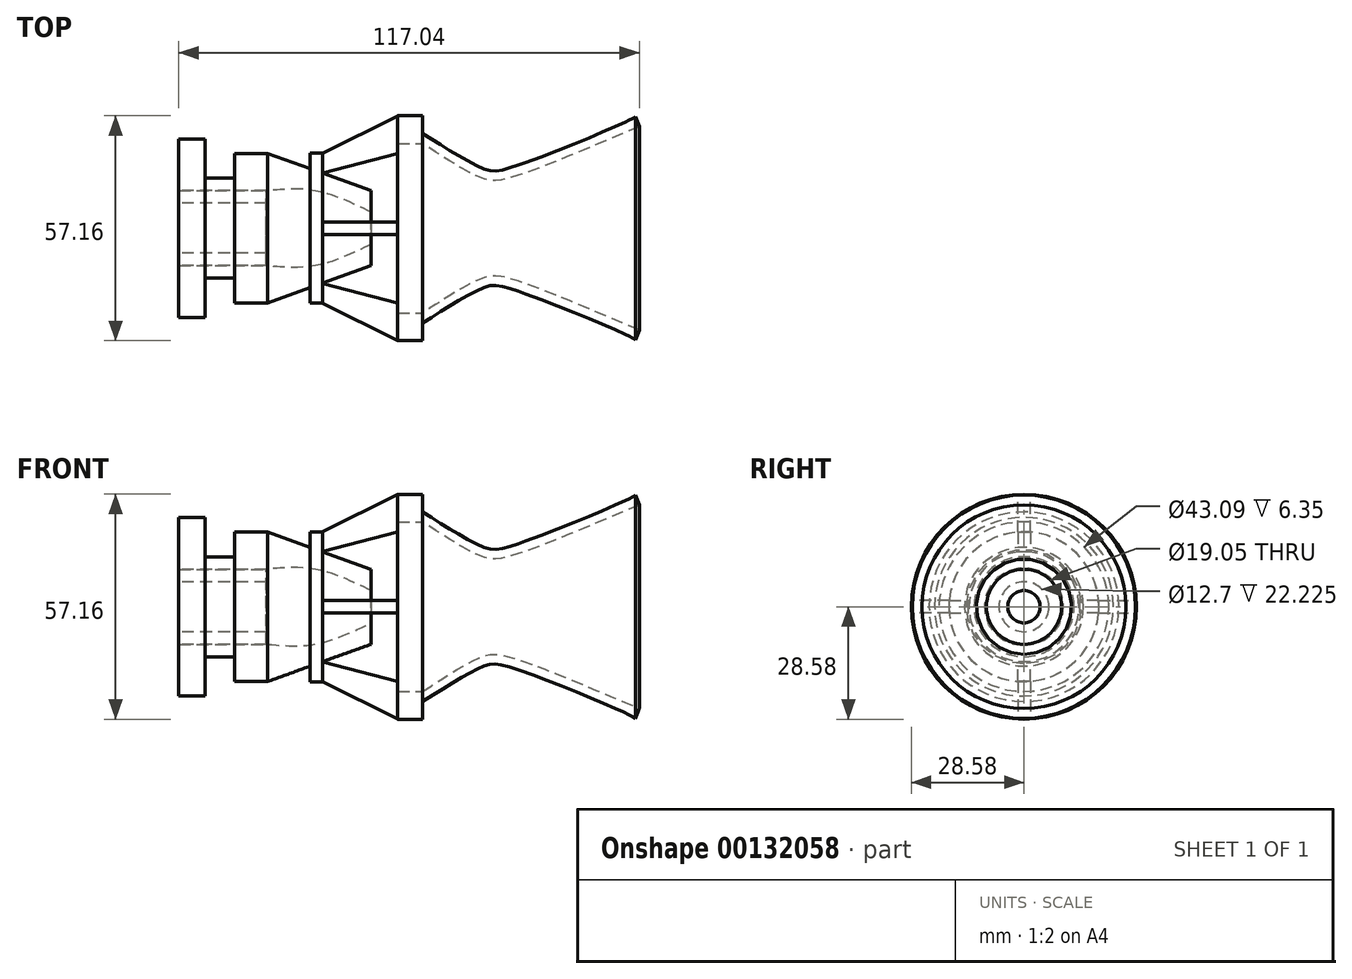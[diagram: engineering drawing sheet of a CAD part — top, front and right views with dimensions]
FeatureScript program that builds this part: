
annotation { "Feature Type Name" : "Feature", "Feature Type Description" : "" }
export const myFeature = defineFeature(function(context is Context, id is Id, definition is map)
    precondition{}
    {
        {
            var Q0;
            Q0=qCreatedBy(makeId("Front.planeOp"),FACE);
            var sketch = newSketch(context, id + "F0", { "sketchPlane" : qUnion([Q0])});
            skPoint(sketch, "E0.middle", {"position": v(0, 0) * mm});
            skLineSegment(sketch, "E1", {"start": v(0, 0) * mm, "end": v(0, 21.54) * mm, "construction": true});
            skPoint(sketch, "E2", {"position": v(0, 21.54) * mm});
            skPoint(sketch, "E3", {"position": v(15.15, 12.7) * mm});
            skPoint(sketch, "E4", {"position": v(21.84, 12.7) * mm});
            skPoint(sketch, "E5", {"position": v(40.5, 25.89) * mm});
            skFitSpline(sketch, "E6", {"points": [v(0, 21.54) * mm, v(15.15, 12.7) * mm, v(21.84, 12.7) * mm, v(55.06, 25.89) * mm], "startDerivative": vector(52.15, -34.15) * mm, "endDerivative": vector(85.37, 36.4) * mm});
            skPoint(sketch, "E7.0.1.0", {"position": v(0, 24.13) * mm});
            skPoint(sketch, "E7.1.1.0", {"position": v(25.4, 24.13) * mm});
            skPoint(sketch, "E7.2.1.0", {"position": v(50.8, 24.13) * mm});
            skLineSegment(sketch, "E7.direction2", {"start": v(0, 24.08) * mm, "end": v(0, 24.13) * mm, "construction": true});
            skPoint(sketch, "E8.1.0.0", {"position": v(21.84, 15.24) * mm});
            skPoint(sketch, "E8.1.0.1", {"position": v(50.8, 26.67) * mm});
            skPoint(sketch, "E8.1.0.2", {"position": v(15.15, 15.24) * mm});
            skPoint(sketch, "E8.1.0.3", {"position": v(25.4, 26.67) * mm});
            skPoint(sketch, "E8.1.0.4", {"position": v(40.5, 28.43) * mm});
            skPoint(sketch, "E8.1.0.5", {"position": v(0, 26.67) * mm});
            skPoint(sketch, "E8.1.0.6", {"position": v(0, 24.08) * mm});
            skLineSegment(sketch, "E8.1.0.7", {"start": v(0, 24.08) * mm, "end": v(0, 26.67) * mm, "construction": true});
            skFitSpline(sketch, "E9", {"points": [v(0, 24.08) * mm, v(15.15, 15.24) * mm, v(21.84, 15.24) * mm, v(50.8, 26.67) * mm, v(54.12, 28.35) * mm], "startDerivative": vector(59.62, -37.76) * mm, "endDerivative": vector(15.17, 8.75) * mm});
            skLineSegment(sketch, "E10", {"start": v(54.12, 28.35) * mm, "end": v(55.06, 25.89) * mm});
            skLineSegment(sketch, "E11", {"start": v(0, 0) * mm, "end": v(0, 21.54) * mm});
            skLineSegment(sketch, "E12", {"start": v(0, 28.58) * mm, "end": v(-6.35, 28.58) * mm});
            skLineSegment(sketch, "E13", {"start": v(-6.35, 28.58) * mm, "end": v(-6.35, 21.54) * mm});
            skLineSegment(sketch, "E14", {"start": v(-6.35, 21.54) * mm, "end": v(0, 21.54) * mm});
            skLineSegment(sketch, "E15", {"start": v(-25.4, 19.05) * mm, "end": v(-28.58, 19.05) * mm});
            skLineSegment(sketch, "E16", {"start": v(-28.58, 19.05) * mm, "end": v(-28.58, 15.1) * mm});
            skPoint(sketch, "E17.startSnap0", {"position": v(-28.58, 9.53) * mm});
            skLineSegment(sketch, "E18", {"start": v(-39.44, 19.02) * mm, "end": v(-47.76, 19.02) * mm});
            skLineSegment(sketch, "E19", {"start": v(-47.76, 19.02) * mm, "end": v(-47.76, 12.7) * mm});
            skLineSegment(sketch, "E20", {"start": v(-47.76, 12.7) * mm, "end": v(-55.22, 12.7) * mm});
            skLineSegment(sketch, "E21", {"start": v(-55.22, 12.7) * mm, "end": v(-55.22, 22.7) * mm});
            skLineSegment(sketch, "E22", {"start": v(-55.22, 22.7) * mm, "end": v(-61.98, 22.7) * mm});
            skLineSegment(sketch, "E23", {"start": v(-61.98, 22.7) * mm, "end": v(-61.98, 12.7) * mm});
            skLineSegment(sketch, "E24", {"start": v(-61.98, 12.7) * mm, "end": v(-61.98, 9.53) * mm});
            skLineSegment(sketch, "E25", {"start": v(-61.98, 9.53) * mm, "end": v(-39.44, 9.53) * mm});
            skPoint(sketch, "E26.1.internal.snap0", {"position": v(-25.4, 9.53) * mm});
            skFitSpline(sketch, "E26", {"points": [v(-39.44, 9.53) * mm, v(-27.3, 9.53) * mm, v(-13.09, 4.11) * mm], "startDerivative": vector(25.44, 2.42) * mm, "endDerivative": vector(27.23, -12.96) * mm});
            skLineSegment(sketch, "E27", {"start": v(-13.09, 4.11) * mm, "end": v(-13.09, 9.53) * mm});
            skLineSegment(sketch, "E28", {"start": v(-13.09, 9.53) * mm, "end": v(-25.4, 13.96) * mm});
            skLineSegment(sketch, "E29.trimOffspring", {"start": v(-25.4, 13.96) * mm, "end": v(-25.4, 19.05) * mm});
            skPoint(sketch, "E30.end.orphan", {"position": v(-25.4, 0) * mm});
            skPoint(sketch, "E30.start.orphan", {"position": v(-28.58, 0) * mm});
            skPoint(sketch, "E0.left.start.orphan", {"position": v(89, 12.7) * mm});
            skPoint(sketch, "E0.top.start.orphan", {"position": v(89, -12.7) * mm});
            skPoint(sketch, "E0.right.end.orphan", {"position": v(-89, -12.7) * mm});
            skPoint(sketch, "E0.right.start.orphan", {"position": v(-89, 12.7) * mm});
            skLineSegment(sketch, "E31.trimOffspring", {"start": v(-28.58, 15.1) * mm, "end": v(-39.44, 19.02) * mm});
            skLineSegment(sketch, "E32.trimOffspring", {"start": v(0, 24.08) * mm, "end": v(0, 72.25) * mm, "construction": true});
            skLineSegment(sketch, "E33.trimOffspring", {"start": v(0, 24.08) * mm, "end": v(0, 28.58) * mm});
            skLineSegment(sketch, "E34", {"start": v(0, 0) * mm, "end": v(-43.22, 0) * mm, "construction": true});
            skSolve(sketch);
        }
        {
            var Q0;
            Q0 = qSketchRegion(id + "F0", true);
            var Q1;
            Q1=sQuery(id+"F0.wireOp",EDGE,"E34");
            revolve(context, id + "F1", {"entities" : qUnion([Q0]), "axis" : qUnion([Q1]), "revolveType" : RevolveType.FULL});
        }
        {
            var Q0;
            Q0=qCreatedBy(makeId("Front.planeOp"),FACE);
            var sketch = newSketch(context, id + "F2", { "sketchPlane" : qUnion([Q0])});
            skLineSegment(sketch, "E35", {"start": v(-25.5, 18.96) * mm, "end": v(-6.24, 28.52) * mm});
            skLineSegment(sketch, "E36", {"start": v(-25.5, 18.96) * mm, "end": v(-25.5, 14.05) * mm});
            skLineSegment(sketch, "E37", {"start": v(-25.5, 14.05) * mm, "end": v(-6.37, 18.96) * mm});
            skLineSegment(sketch, "E38", {"start": v(-6.37, 18.96) * mm, "end": v(-6.24, 28.52) * mm});
            skSolve(sketch);
        }
        {
            var Q0;
            Q0 = qSketchRegion(id + "F2", true);
            extrude(context, id + "F3", {"entities" : qUnion([Q0]), "endBound" : BoundingType.SYMMETRIC, "depth" : 3.17 * mm});
        }
        {
            var Q0;
            Q0=makeQuery(id+"F3.opExtrude","SWEPT_BODY",BODY,{"disambiguationData":[OSD([sQuery(id+"F2.wireOp",EDGE,"E35"),sQuery(id+"F2.wireOp",EDGE,"E36"),sQuery(id+"F2.wireOp",EDGE,"E37"),sQuery(id+"F2.wireOp",EDGE,"E38")])]});
            var Q1;
            Q1=sQuery(id+"F0.wireOp",EDGE,"E34");
            circularPattern(context, id + "F4", {"entities" : qUnion([Q0]), "axis" : qUnion([Q1]), "angle" : 360 * degree, "instanceCount" : 4, "equalSpace" : true});
        }
        {
            var Q0;
            Q0=makeQuery(id+"F1.opRevolve","SWEPT_FACE",FACE,{"disambiguationData":[OSD([sQuery(id+"F0.wireOp",EDGE,"E23"),sQuery(id+"F0.wireOp",EDGE,"E24")])]});
            var sketch = newSketch(context, id + "F5", { "sketchPlane" : qUnion([Q0])});
            skCircle(sketch, "E39", {"center": v(0, 0) * mm, "radius": 6.35 * mm});
            skCircle(sketch, "E40", {"center": v(0, 0) * mm, "radius": 9.53 * mm});
            skSolve(sketch);
        }
        {
            var Q0;
            Q0 = qSketchRegion(id + "F5", true);
            extrude(context, id + "F6", {"entities" : qUnion([Q0]), "oppositeDirection" : true, "depth" : 22.22 * mm});
        }
    });
